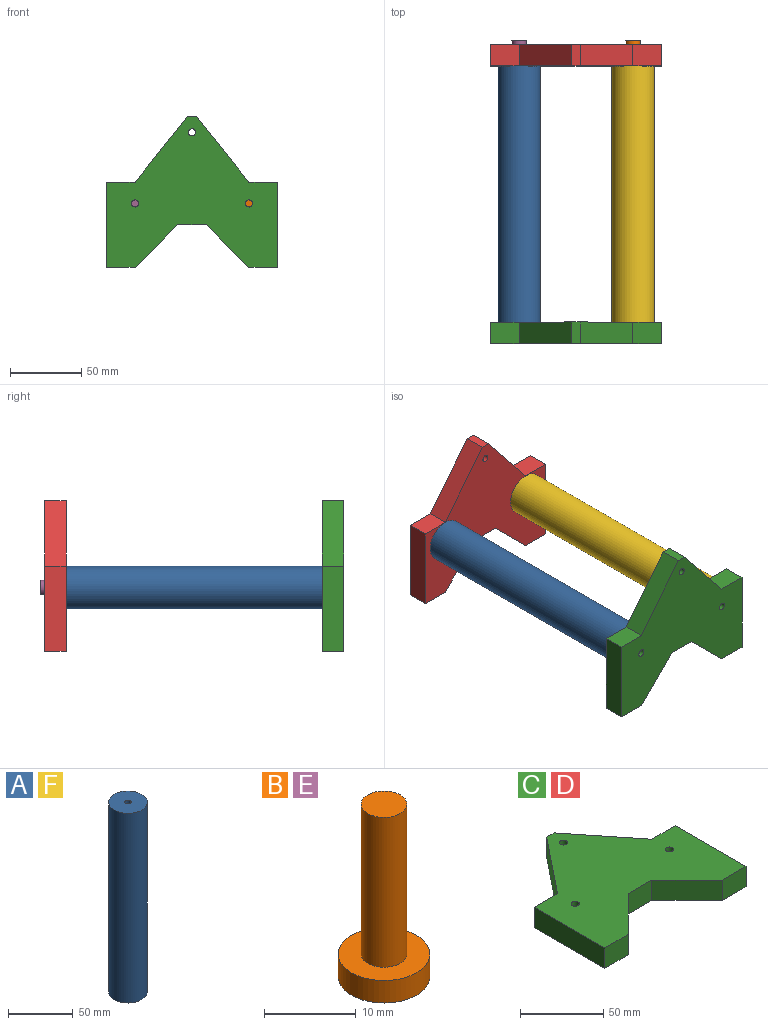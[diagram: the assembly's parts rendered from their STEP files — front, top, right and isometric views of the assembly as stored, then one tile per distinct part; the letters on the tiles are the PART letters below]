
ASSEMBLY  parts=6 mates=11
PART A: 4 faces, bbox 30x30x180 mm
  f0: cylinder r=15mm len=180mm, axis (0,0,-1), area 16964.6mm2, adj f1,f2
  f1: plane 30x30mm, normal (0,0,1), area 687.2mm2, adj f0,f3
  f2: plane 30x30mm, normal (0,0,-1), area 687.2mm2, adj f0,f3
  f3: cylinder r=2.5mm len=180mm, axis (0,0,1), area 2827.4mm2, adj f1,f2
PART B: 5 faces, bbox 10x10x23 mm
  f0: cylinder r=5mm len=10mm, axis (0,0,-1), area 94.2mm2, adj f1,f2
  f1: plane 10x10mm, normal (0,0,1), area 58.9mm2, adj f0,f3
  f2: plane 10x10mm, normal (0,0,-1), area 78.5mm2, adj f0
  f3: cylinder r=2.5mm len=20mm, axis (0,0,-1), area 314.2mm2, adj f1,f4
  f4: plane 5x5mm, normal (0,0,1), area 19.6mm2, adj f3
PART C: 17 faces, bbox 120x106.1x15 mm
  f0: plane 20x15mm, normal (0,1,0), area 300mm2, adj f7,f11,f12,f14
  f1: plane 60x15mm, normal (-1,0,0), area 900mm2, adj f2,f10,f11,f12
  f2: plane 20x15mm, normal (0,-1,0), area 300mm2, adj f1,f3,f11,f12
  f3: plane 30x30mm, normal (0.71,-0.71,0), area 636.4mm2, adj f2,f4,f11,f12
  f4: plane 20x15mm, normal (0,-1,0), area 300mm2, adj f3,f5,f11,f12
  f5: plane 30x30mm, normal (-0.71,-0.71,0), area 636.4mm2, adj f4,f6,f11,f12
  f6: plane 20x15mm, normal (0,-1,0), area 300mm2, adj f5,f7,f11,f12
  f7: plane 60x15mm, normal (1,0,0), area 900mm2, adj f0,f6,f11,f12
  f8: cylinder r=2.5mm len=15mm, axis (0,0,-1), area 235.6mm2, adj f11,f12
  f9: cylinder r=2.5mm len=15mm, axis (0,0,-1), area 235.6mm2, adj f11,f12
  f10: plane 20x15mm, normal (0,1,0), area 300mm2, adj f1,f11,f12,f13
  f11: plane 120x106.1mm, normal (0,0,1), area 7628.9mm2, adj f0,f1,f2,f3,f4,f5,f6,f7
  f12: plane 120x106.1mm, normal (0,0,-1), area 7628.9mm2, adj f0,f1,f2,f3,f4,f5,f6,f7
  f13: plane 46.1x36.88mm, normal (-0.78,0.62,0), area 885.5mm2, adj f10,f11,f12,f16
  f14: plane 46.1x36.88mm, normal (0.78,0.62,0), area 885.5mm2, adj f0,f11,f12,f16
  f15: cylinder r=2.5mm len=15mm, axis (0,0,-1), area 235.6mm2, adj f11,f12
  f16: plane 15x6.25mm, normal (0,1,0), area 93.7mm2, adj f11,f12,f13,f14
PART D: same geometry as C
PART E: same geometry as B
PART F: same geometry as A
PLACE A rot(axis=(1,0,0),90deg) t=(1.61,62.35,53.92)mm
PLACE B rot(axis=(1,0,0),90deg) t=(81.61,80.35,53.92)mm
PLACE C rot(axis=(0,0.71,0.71),180deg) t=(101.61,-132.65,8.92)mm
PLACE D rot(axis=(1,0,0),90deg) t=(-18.39,77.35,8.92)mm
PLACE E rot(axis=(1,0,0),90deg) t=(1.61,80.35,53.92)mm
PLACE F rot(axis=(-1,0,0),90deg) t=(81.61,-117.65,53.92)mm
MATE planar A.f0 <-> D.f11  axis (0,1,0) through (1.61,62.35,53.92)mm
MATE planar C.f11 <-> F.f0  axis (0,1,0) through (41.61,-117.65,54.33)mm
MATE cylindrical C.f8 <-> F.f0  axis (0,1,0) through (81.61,-117.65,53.92)mm
MATE cylindrical C.f9 <-> A.f0  axis (0,1,0) through (1.61,-117.65,53.92)mm
MATE cylindrical E.f3 <-> D.f8  axis (0,1,0) through (1.61,67.35,53.92)mm
MATE cylindrical F.f0 <-> D.f9  axis (0,1,0) through (81.61,62.35,53.92)mm
MATE cylindrical B.f3 <-> D.f9  axis (0,1,0) through (81.61,67.35,53.92)mm
MATE planar B.f0 <-> D.f12  axis (0,-1,0) through (81.61,77.35,53.92)mm
MATE planar E.f0 <-> D.f12  axis (0,-1,0) through (1.61,77.35,53.92)mm
MATE cylindrical A.f0 <-> D.f8  axis (0,1,0) through (1.61,62.35,53.92)mm
MATE planar F.f0 <-> D.f11  axis (0,1,0) through (81.61,62.35,53.92)mm
